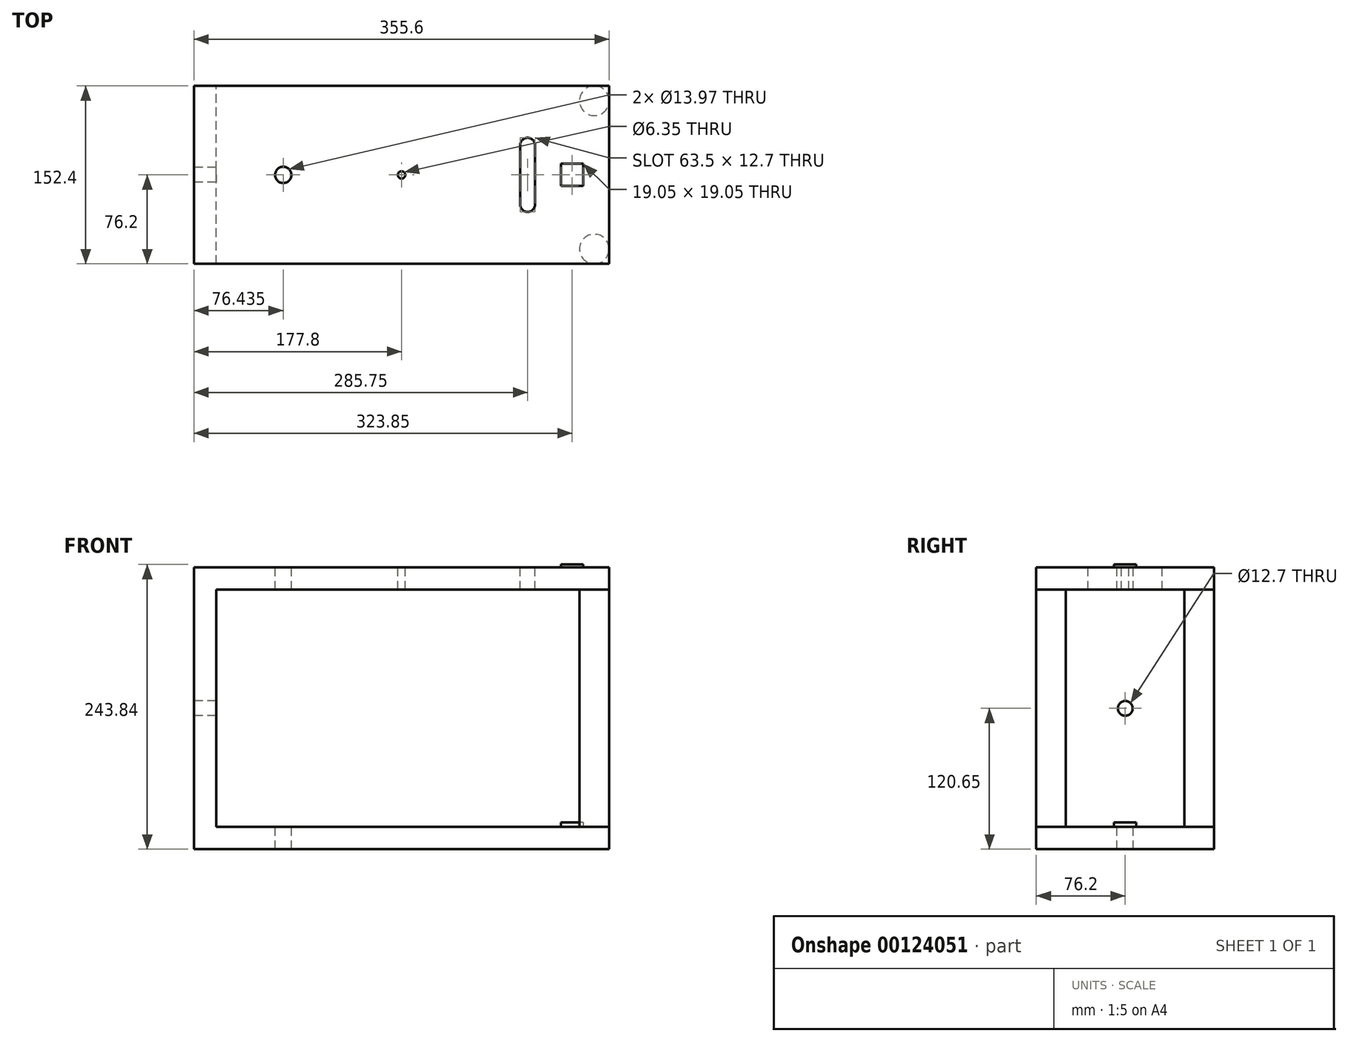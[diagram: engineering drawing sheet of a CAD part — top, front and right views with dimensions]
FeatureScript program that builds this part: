
annotation { "Feature Type Name" : "Feature", "Feature Type Description" : "" }
export const myFeature = defineFeature(function(context is Context, id is Id, definition is map)
    precondition{}
    {
        {
            var Q0;
            Q0=qCreatedBy(makeId("Top.planeOp"),FACE);
            var sketch = newSketch(context, id + "F0", { "sketchPlane" : qUnion([Q0])});
            skLineSegment(sketch, "E0.bottom", {"start": v(177.8, 76.2) * mm, "end": v(-177.8, 76.2) * mm});
            skLineSegment(sketch, "E0.top", {"start": v(177.8, -76.2) * mm, "end": v(-177.8, -76.2) * mm});
            skLineSegment(sketch, "E0.left", {"start": v(177.8, 76.2) * mm, "end": v(177.8, -76.2) * mm});
            skLineSegment(sketch, "E0.right", {"start": v(-177.8, 76.2) * mm, "end": v(-177.8, -76.2) * mm});
            skPoint(sketch, "E0.middle", {"position": v(0, 0) * mm});
            skSolve(sketch);
        }
        {
            var Q0;
            Q0 = qSketchRegion(id + "F0", true);
            extrude(context, id + "F1", {"entities" : qUnion([Q0]), "depth" : 19.05 * mm});
        }
        {
            var Q0;
            Q0=makeQuery(id+"F1.opExtrude","CAP_FACE",FACE,{"disambiguationData":[OSD([sQuery(id+"F0.wireOp",EDGE,"E0.bottom"),sQuery(id+"F0.wireOp",EDGE,"E0.top"),sQuery(id+"F0.wireOp",EDGE,"E0.left"),sQuery(id+"F0.wireOp",EDGE,"E0.right")])],"isStart":false});
            var sketch = newSketch(context, id + "F2", { "sketchPlane" : qUnion([Q0])});
            skLineSegment(sketch, "E1.bottom", {"start": v(-177.8, 76.2) * mm, "end": v(-158.75, 76.2) * mm});
            skLineSegment(sketch, "E1.top", {"start": v(-177.8, -76.2) * mm, "end": v(-158.75, -76.2) * mm});
            skLineSegment(sketch, "E1.left", {"start": v(-177.8, 76.2) * mm, "end": v(-177.8, -76.2) * mm});
            skLineSegment(sketch, "E1.right", {"start": v(-158.75, 76.2) * mm, "end": v(-158.75, -76.2) * mm});
            skSolve(sketch);
        }
        {
            var Q0;
            Q0=makeQuery(id+"F2.imprint","IMPRINT",FACE,{"disambiguationData":[TD([[makeQuery(id+"F2.imprint","IMPRINT",EDGE,{"derivedFrom":sQuery(id+"F2.wireOp",EDGE,"E1.bottom")}),1.0]])]});
            extrude(context, id + "F3", {"entities" : qUnion([Q0]), "operationType" : NewBodyOperationType.ADD, "depth" : 222.25 * mm});
        }
        {
            var Q0;
            Q0=makeQuery(id+"F1.opExtrude","CAP_FACE",FACE,{"disambiguationData":[OSD([sQuery(id+"F0.wireOp",EDGE,"E0.bottom"),sQuery(id+"F0.wireOp",EDGE,"E0.top"),sQuery(id+"F0.wireOp",EDGE,"E0.left"),sQuery(id+"F0.wireOp",EDGE,"E0.right")])],"isStart":false});
            var sketch = newSketch(context, id + "F4", { "sketchPlane" : qUnion([Q0])});
            skLineSegment(sketch, "E2", {"start": v(177.8, -76.2) * mm, "end": v(165.1, -76.2) * mm, "construction": true});
            skLineSegment(sketch, "E3", {"start": v(165.1, -76.2) * mm, "end": v(165.1, 76.2) * mm, "construction": true});
            skLineSegment(sketch, "E4", {"start": v(177.8, -76.2) * mm, "end": v(177.8, -63.5) * mm, "construction": true});
            skLineSegment(sketch, "E5", {"start": v(177.8, -63.5) * mm, "end": v(165.1, -63.5) * mm, "construction": true});
            skLineSegment(sketch, "E6", {"start": v(177.8, 76.2) * mm, "end": v(177.8, 63.5) * mm, "construction": true});
            skLineSegment(sketch, "E7", {"start": v(177.8, 63.5) * mm, "end": v(165.1, 63.5) * mm, "construction": true});
            skCircle(sketch, "E8", {"center": v(165.1, 63.5) * mm, "radius": 12.7 * mm});
            skCircle(sketch, "E9", {"center": v(165.1, -63.5) * mm, "radius": 12.7 * mm});
            skSolve(sketch);
        }
        {
            var Q0;
            {var subQ0=sQuery(id+"F4.wireOp",EDGE,"E8");var subQ1=makeQuery(id+"F4.imprint","INTERSECT",VERTEX,{"derivedFrom":[makeQuery(id+"F1.opExtrude","CAP_EDGE",EDGE,{"disambiguationData":[OSD([sQuery(id+"F0.wireOp",EDGE,"E0.left")])],"isStart":false}),subQ0]});Q0=makeQuery(id+"F4.imprint","IMPRINT",FACE,{"disambiguationData":[TD([[makeQuery(id+"F4.imprint","IMPRINT",EDGE,{"disambiguationData":[TD([[subQ1,-1.0]])],"derivedFrom":subQ0}),1.0]])]});}
            var Q1;
            {var subQ0=sQuery(id+"F4.wireOp",EDGE,"E9");var subQ1=makeQuery(id+"F4.imprint","INTERSECT",VERTEX,{"derivedFrom":[makeQuery(id+"F1.opExtrude","CAP_EDGE",EDGE,{"disambiguationData":[OSD([sQuery(id+"F0.wireOp",EDGE,"E0.left")])],"isStart":false}),subQ0]});Q1=makeQuery(id+"F4.imprint","IMPRINT",FACE,{"disambiguationData":[TD([[makeQuery(id+"F4.imprint","IMPRINT",EDGE,{"disambiguationData":[TD([[subQ1,-1.0]])],"derivedFrom":subQ0}),1.0]])]});}
            extrude(context, id + "F5", {"entities" : qUnion([Q0, Q1]), "operationType" : NewBodyOperationType.ADD, "depth" : 184.15 * mm});
        }
        {
            var Q0;
            Q0=makeQuery(id+"F3.opExtrude","SWEPT_FACE",FACE,{"disambiguationData":[OSD([sQuery(id+"F2.wireOp",EDGE,"E1.right")])]});
            var sketch = newSketch(context, id + "F6", { "sketchPlane" : qUnion([Q0])});
            skLineSegment(sketch, "E10.bottom", {"start": v(-76.2, 241.3) * mm, "end": v(76.2, 241.3) * mm});
            skLineSegment(sketch, "E10.top", {"start": v(-76.2, 222.25) * mm, "end": v(76.2, 222.25) * mm});
            skLineSegment(sketch, "E10.left", {"start": v(-76.2, 241.3) * mm, "end": v(-76.2, 222.25) * mm});
            skLineSegment(sketch, "E10.right", {"start": v(76.2, 241.3) * mm, "end": v(76.2, 222.25) * mm});
            skSolve(sketch);
        }
        {
            var Q0;
            Q0 = qSketchRegion(id + "F6", true);
            extrude(context, id + "F7", {"entities" : qUnion([Q0]), "operationType" : NewBodyOperationType.ADD, "depth" : 336.55 * mm});
        }
        {
            var Q0;
            Q0=makeQuery(id+"F5.opExtrude","CAP_FACE",FACE,{"disambiguationData":[OSD([sQuery(id+"F4.wireOp",EDGE,"E8")])],"isStart":false});
            var Q1;
            Q1=makeQuery(id+"F5.opExtrude","CAP_FACE",FACE,{"disambiguationData":[OSD([sQuery(id+"F4.wireOp",EDGE,"E9")])],"isStart":false});
            var Q2;
            Q2=makeQuery(id+"F5.opExtrude","CAP_FACE",FACE,{"disambiguationData":[OSD([sQuery(id+"F4.wireOp",EDGE,"E8")])],"isStart":false});
            extrude(context, id + "F8", {"entities" : qUnion([Q0, Q1]), "operationType" : NewBodyOperationType.ADD, "endBoundEntityFace" : qUnion([Q2]), "depth" : 25.4 * mm});
        }
        {
            var Q0;
            Q0=makeQuery(id+"F3.boolean.opBoolean","MERGE",FACE,{"derivedFrom":[makeQuery(id+"F1.opExtrude","SWEPT_FACE",FACE,{"disambiguationData":[OSD([sQuery(id+"F0.wireOp",EDGE,"E0.right")])]}),makeQuery(id+"F3.opExtrude","SWEPT_FACE",FACE,{"disambiguationData":[OSD([sQuery(id+"F2.wireOp",EDGE,"E1.left")])]})]});
            var sketch = newSketch(context, id + "F9", { "sketchPlane" : qUnion([Q0])});
            skLineSegment(sketch, "E11.bottom", {"start": v(-76.2, 241.3) * mm, "end": v(76.2, 241.3) * mm, "construction": true});
            skLineSegment(sketch, "E11.top", {"start": v(-76.2, 222.25) * mm, "end": v(76.2, 222.25) * mm, "construction": true});
            skLineSegment(sketch, "E11.left", {"start": v(-76.2, 241.3) * mm, "end": v(-76.2, 222.25) * mm, "construction": true});
            skLineSegment(sketch, "E11.right", {"start": v(76.2, 241.3) * mm, "end": v(76.2, 222.25) * mm, "construction": true});
            skLineSegment(sketch, "E12.bottom", {"start": v(76.2, 0) * mm, "end": v(-76.2, 0) * mm, "construction": true});
            skLineSegment(sketch, "E12.top", {"start": v(76.2, 19.05) * mm, "end": v(-76.2, 19.05) * mm, "construction": true});
            skLineSegment(sketch, "E12.left", {"start": v(76.2, 0) * mm, "end": v(76.2, 19.05) * mm, "construction": true});
            skLineSegment(sketch, "E12.right", {"start": v(-76.2, 0) * mm, "end": v(-76.2, 19.05) * mm, "construction": true});
            skLineSegment(sketch, "E13", {"start": v(0, 19.05) * mm, "end": v(0, 120.65) * mm, "construction": true});
            skCircle(sketch, "E14", {"center": v(0, 120.65) * mm, "radius": 6.35 * mm});
            skSolve(sketch);
        }
        {
            var Q0;
            Q0=makeQuery(id+"F9.imprint","IMPRINT",FACE,{"disambiguationData":[TD([[makeQuery(id+"F9.imprint","IMPRINT",EDGE,{"derivedFrom":sQuery(id+"F9.wireOp",EDGE,"E14")}),1.0]])]});
            var Q1;
            Q1=sQuery(id+"F9.wireOp",EDGE,"E14");
            extrude(context, id + "F10", {"entities" : qUnion([Q0]), "operationType" : NewBodyOperationType.REMOVE, "surfaceEntities" : qUnion([Q1]), "oppositeDirection" : true, "depth" : 25.4 * mm});
        }
        {
            var Q0;
            Q0=makeQuery(id+"F7.boolean.opBoolean","MERGE",FACE,{"derivedFrom":[makeQuery(id+"F3.opExtrude","CAP_FACE",FACE,{"disambiguationData":[OSD([sQuery(id+"F2.wireOp",EDGE,"E1.bottom"),sQuery(id+"F2.wireOp",EDGE,"E1.top"),sQuery(id+"F2.wireOp",EDGE,"E1.left"),sQuery(id+"F2.wireOp",EDGE,"E1.right")])],"isStart":false}),makeQuery(id+"F7.opExtrude","SWEPT_FACE",FACE,{"disambiguationData":[OSD([sQuery(id+"F6.wireOp",EDGE,"E10.bottom")])]})]});
            var sketch = newSketch(context, id + "F11", { "sketchPlane" : qUnion([Q0])});
            skLineSegment(sketch, "E15.bottom", {"start": v(38.1, 38.1) * mm, "end": v(-38.1, 38.1) * mm, "construction": true});
            skLineSegment(sketch, "E15.top", {"start": v(38.1, -38.1) * mm, "end": v(-38.1, -38.1) * mm, "construction": true});
            skLineSegment(sketch, "E15.left", {"start": v(38.1, 38.1) * mm, "end": v(38.1, -38.1) * mm, "construction": true});
            skLineSegment(sketch, "E15.right", {"start": v(-38.1, 38.1) * mm, "end": v(-38.1, -38.1) * mm, "construction": true});
            skPoint(sketch, "E15.middle", {"position": v(0, 0) * mm});
            skLineSegment(sketch, "E16", {"start": v(0, 0) * mm, "end": v(107.95, 0) * mm, "construction": true});
            skPoint(sketch, "E16.endSnap0", {"position": v(38.1, 0) * mm});
            skLineSegment(sketch, "E17", {"start": v(0, 0) * mm, "end": v(-50.8, 0) * mm, "construction": true});
            skCircle(sketch, "E18", {"center": v(0, 0) * mm, "radius": 3.18 * mm});
            skCircle(sketch, "E19", {"center": v(0, 0) * mm, "radius": 50.8 * mm, "construction": true});
            skCircle(sketch, "E20", {"center": v(107.95, 0) * mm, "radius": 25.4 * mm, "construction": true});
            skLineSegment(sketch, "E21", {"start": v(0, 0) * mm, "end": v(-101.6, 0) * mm, "construction": true});
            skCircle(sketch, "E22", {"center": v(-101.6, 0) * mm, "radius": 25.4 * mm, "construction": true});
            skSolve(sketch);
        }
        {
            var Q0;
            Q0=makeQuery(id+"F11.imprint","IMPRINT",FACE,{"disambiguationData":[TD([[makeQuery(id+"F11.imprint","IMPRINT",EDGE,{"derivedFrom":sQuery(id+"F11.wireOp",EDGE,"E18")}),-1.0]])]});
            var sketch = newSketch(context, id + "F12", { "sketchPlane" : qUnion([Q0])});
            skPoint(sketch, "E23.0", {"position": v(107.95, 0) * mm});
            skLineSegment(sketch, "E24", {"start": v(107.95, 0) * mm, "end": v(107.95, -25.4) * mm, "construction": true});
            skLineSegment(sketch, "E25", {"start": v(107.95, -25.4) * mm, "end": v(107.95, 0) * mm, "construction": true});
            skLineSegment(sketch, "E26", {"start": v(107.95, 0) * mm, "end": v(107.95, 25.4) * mm, "construction": true});
            skArc(sketch, "E27", {"start": v(114.3, 25.4) * mm, "mid": v(107.95, 31.75) * mm, "end": v(101.6, 25.4) * mm});
            skArc(sketch, "E28.MirrorCS", {"start": v(114.3, -25.4) * mm, "mid": v(107.95, -31.75) * mm, "end": v(101.6, -25.4) * mm});
            skLineSegment(sketch, "E29", {"start": v(101.6, 25.4) * mm, "end": v(101.6, -25.4) * mm});
            skLineSegment(sketch, "E30", {"start": v(114.3, 25.4) * mm, "end": v(114.3, -25.4) * mm});
            skSolve(sketch);
        }
        {
            var Q0;
            Q0 = qSketchRegion(id + "F12", true);
            var Q1;
            Q1=sQuery(id+"F12.wireOp",EDGE,"E27");
            var Q2;
            Q2=sQuery(id+"F12.wireOp",EDGE,"E29");
            var Q3;
            Q3=sQuery(id+"F12.wireOp",EDGE,"E30");
            var Q4;
            Q4=sQuery(id+"F12.wireOp",EDGE,"E28.MirrorCS");
            extrude(context, id + "F13", {"entities" : qUnion([Q0]), "operationType" : NewBodyOperationType.REMOVE, "surfaceEntities" : qUnion([Q1, Q2, Q3, Q4]), "oppositeDirection" : true, "depth" : 19.05 * mm});
        }
        {
            var Q0;
            Q0=makeQuery(id+"F11.imprint","IMPRINT",FACE,{"disambiguationData":[TD([[makeQuery(id+"F11.imprint","IMPRINT",EDGE,{"derivedFrom":sQuery(id+"F11.wireOp",EDGE,"E18")}),-1.0]])]});
            var sketch = newSketch(context, id + "F14", { "sketchPlane" : qUnion([Q0])});
            skSolve(sketch);
        }
        {
            var Q0;
            Q0=makeQuery(id+"F14.imprint","IMPRINT",FACE,{"disambiguationData":[TD([[makeQuery(id+"F14.imprint","IMPRINT",EDGE,{"derivedFrom":makeQuery(id+"F11.imprint","IMPRINT",EDGE,{"derivedFrom":sQuery(id+"F11.wireOp",EDGE,"E18")})}),1.0]])]});
            var sketch = newSketch(context, id + "F15", { "sketchPlane" : qUnion([Q0])});
            skSolve(sketch);
        }
        {
            var Q0;
            Q0 = qSketchRegion(id + "F15", true);
            var Q1;
            Q1=makeQuery(id+"F14.imprint","IMPRINT",FACE,{"disambiguationData":[TD([[makeQuery(id+"F14.imprint","IMPRINT",EDGE,{"derivedFrom":makeQuery(id+"F11.imprint","IMPRINT",EDGE,{"derivedFrom":sQuery(id+"F11.wireOp",EDGE,"E18")})}),1.0]])]});
            extrude(context, id + "F16", {"entities" : qUnion([Q0, Q1]), "operationType" : NewBodyOperationType.REMOVE, "oppositeDirection" : true, "depth" : 19.05 * mm});
        }
        {
            var Q0;
            {var subQ0=sQuery(id+"F0.wireOp",EDGE,"E0.left");var subQ1=sQuery(id+"F0.wireOp",EDGE,"E0.top");var subQ2=sQuery(id+"F0.wireOp",EDGE,"E0.bottom");var subQ3=makeQuery(id+"F1.opExtrude","CAP_FACE",FACE,{"disambiguationData":[OSD([subQ2,subQ1,subQ0,sQuery(id+"F0.wireOp",EDGE,"E0.right")])],"isStart":false});Q0=makeQuery(id+"F5.boolean.opBoolean","SPLIT",FACE,{"disambiguationData":[TD([makeQuery(id+"F1.opExtrude","SWEPT_FACE",FACE,{"disambiguationData":[OSD([subQ2])]}),subQ3,makeQuery(id+"F1.opExtrude","SWEPT_FACE",FACE,{"disambiguationData":[OSD([subQ1])]}),makeQuery(id+"F1.opExtrude","SWEPT_FACE",FACE,{"disambiguationData":[OSD([subQ0])]}),makeQuery(id+"F3.opExtrude","SWEPT_FACE",FACE,{"disambiguationData":[OSD([sQuery(id+"F2.wireOp",EDGE,"E1.bottom")])]}),makeQuery(id+"F3.opExtrude","SWEPT_FACE",FACE,{"disambiguationData":[OSD([sQuery(id+"F2.wireOp",EDGE,"E1.top")])]}),makeQuery(id+"F3.opExtrude","SWEPT_FACE",FACE,{"disambiguationData":[OSD([sQuery(id+"F2.wireOp",EDGE,"E1.right")])]}),makeQuery(id+"F5.opExtrude","SWEPT_FACE",FACE,{"disambiguationData":[OSD([sQuery(id+"F4.wireOp",EDGE,"E8")])]}),makeQuery(id+"F5.opExtrude","SWEPT_FACE",FACE,{"disambiguationData":[OSD([sQuery(id+"F4.wireOp",EDGE,"E9")])]})])],"derivedFrom":subQ3});}
            var sketch = newSketch(context, id + "F17", { "sketchPlane" : qUnion([Q0])});
            skPoint(sketch, "E31", {"position": v(146.05, 0) * mm});
            skLineSegment(sketch, "E32.bottom", {"start": v(155.58, 9.52) * mm, "end": v(136.53, 9.52) * mm});
            skLineSegment(sketch, "E32.top", {"start": v(155.58, -9.53) * mm, "end": v(136.53, -9.53) * mm});
            skLineSegment(sketch, "E32.left", {"start": v(155.58, 9.52) * mm, "end": v(155.58, -9.53) * mm});
            skLineSegment(sketch, "E32.right", {"start": v(136.53, 9.52) * mm, "end": v(136.53, -9.53) * mm});
            skSolve(sketch);
        }
        {
            var Q0;
            Q0=makeQuery(id+"F17.imprint","IMPRINT",FACE,{"disambiguationData":[TD([[makeQuery(id+"F17.imprint","IMPRINT",EDGE,{"derivedFrom":sQuery(id+"F17.wireOp",EDGE,"E32.bottom")}),1.0]])]});
            extrude(context, id + "F18", {"entities" : qUnion([Q0]), "operationType" : NewBodyOperationType.ADD, "depth" : 3.8 * mm});
        }
        {
            var Q0;
            Q0=makeQuery(id+"F11.imprint","IMPRINT",FACE,{"disambiguationData":[TD([[makeQuery(id+"F11.imprint","IMPRINT",EDGE,{"derivedFrom":sQuery(id+"F11.wireOp",EDGE,"E18")}),-1.0]])]});
            var sketch = newSketch(context, id + "F19", { "sketchPlane" : qUnion([Q0])});
            skPoint(sketch, "E33.0", {"position": v(107.95, 0) * mm});
            skLineSegment(sketch, "E34", {"start": v(107.95, 0) * mm, "end": v(146.05, 0) * mm, "construction": true});
            skLineSegment(sketch, "E35.bottom", {"start": v(155.58, 9.52) * mm, "end": v(136.53, 9.52) * mm});
            skLineSegment(sketch, "E35.top", {"start": v(155.58, -9.53) * mm, "end": v(136.53, -9.53) * mm});
            skLineSegment(sketch, "E35.left", {"start": v(155.58, 9.52) * mm, "end": v(155.58, -9.53) * mm});
            skLineSegment(sketch, "E35.right", {"start": v(136.53, 9.52) * mm, "end": v(136.53, -9.53) * mm});
            skPoint(sketch, "E35.middle", {"position": v(146.05, 0) * mm});
            skSolve(sketch);
        }
        {
            var Q0;
            Q0 = qSketchRegion(id + "F19", true);
            extrude(context, id + "F20", {"entities" : qUnion([Q0]), "operationType" : NewBodyOperationType.ADD, "depth" : 2.54 * mm});
        }
        {
            var Q0;
            Q0=makeQuery(id+"F11.imprint","IMPRINT",FACE,{"disambiguationData":[TD([[makeQuery(id+"F11.imprint","IMPRINT",EDGE,{"derivedFrom":sQuery(id+"F11.wireOp",EDGE,"E18")}),-1.0]])]});
            var sketch = newSketch(context, id + "F21", { "sketchPlane" : qUnion([Q0])});
            skPoint(sketch, "E36", {"position": v(-101.37, 0) * mm});
            skSolve(sketch);
        }
        {
            var Q0;
            Q0=sQuery(id+"F21.wireOp",VERTEX,"E36");
            var Q1;
            Q1=makeQuery(id+"F1.opExtrude","SWEPT_BODY",BODY,{"disambiguationData":[OSD([sQuery(id+"F0.wireOp",EDGE,"E0.bottom"),sQuery(id+"F0.wireOp",EDGE,"E0.top"),sQuery(id+"F0.wireOp",EDGE,"E0.left"),sQuery(id+"F0.wireOp",EDGE,"E0.right")])]});
            hole(context, id + "F22", {"style" : HoleStyle.SIMPLE, "endStyle" : HoleEndStyle.THROUGH, "holeDiameter" : 13.97 * mm, "locations" : qUnion([Q0]), "scope" : qUnion([Q1]), "isTappedThrough" : true});
        }
    });
